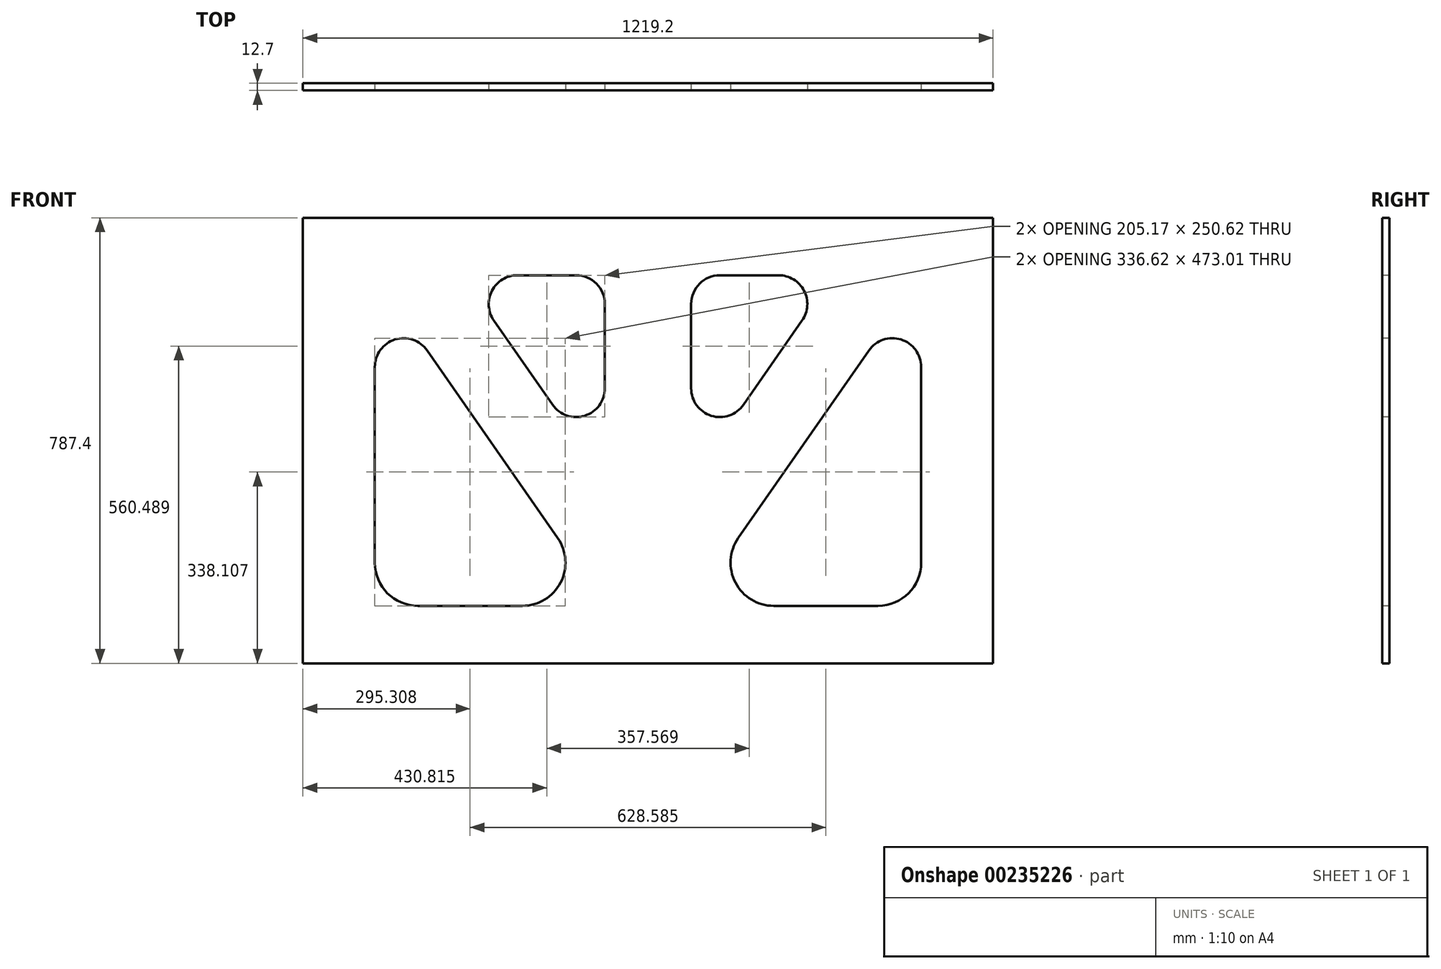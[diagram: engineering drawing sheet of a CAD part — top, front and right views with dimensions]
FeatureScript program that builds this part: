
annotation { "Feature Type Name" : "Feature", "Feature Type Description" : "" }
export const myFeature = defineFeature(function(context is Context, id is Id, definition is map)
    precondition{}
    {
        {
            var Q0;
            Q0=qCreatedBy(makeId("Front.planeOp"),FACE);
            var sketch = newSketch(context, id + "F0", { "sketchPlane" : qUnion([Q0])});
            skLineSegment(sketch, "E0.bottom", {"start": v(-609.6, 393.7) * mm, "end": v(609.6, 393.7) * mm});
            skLineSegment(sketch, "E0.top", {"start": v(-609.6, -393.7) * mm, "end": v(609.6, -393.7) * mm});
            skLineSegment(sketch, "E0.left", {"start": v(-609.6, 393.7) * mm, "end": v(-609.6, -393.7) * mm});
            skLineSegment(sketch, "E0.right", {"start": v(609.6, 393.7) * mm, "end": v(609.6, -393.7) * mm});
            skSolve(sketch);
        }
        {
            var Q0;
            Q0=makeQuery(id+"F0.imprint","IMPRINT",FACE,{"disambiguationData":[TD([[makeQuery(id+"F0.imprint","IMPRINT",EDGE,{"derivedFrom":sQuery(id+"F0.wireOp",EDGE,"E0.bottom")}),-1.0]])]});
            extrude(context, id + "F1", {"entities" : qUnion([Q0]), "depth" : 12.7 * mm});
        }
        {
            var Q0;
            Q0=makeQuery(id+"F1.opExtrude","CAP_FACE",FACE,{"disambiguationData":[OSD([sQuery(id+"F0.wireOp",EDGE,"E0.bottom"),sQuery(id+"F0.wireOp",EDGE,"E0.top"),sQuery(id+"F0.wireOp",EDGE,"E0.left"),sQuery(id+"F0.wireOp",EDGE,"E0.right")])],"isStart":false});
            var sketch = newSketch(context, id + "F2", { "sketchPlane" : qUnion([Q0])});
            skLineSegment(sketch, "E1", {"start": v(-482.6, 130.12) * mm, "end": v(-482.6, -215.9) * mm});
            skLineSegment(sketch, "E2", {"start": v(-406.4, -292.1) * mm, "end": v(-222.03, -292.1) * mm});
            skLineSegment(sketch, "E3", {"start": v(-159.48, -172.38) * mm, "end": v(-390.1, 159.13) * mm});
            skLineSegment(sketch, "E4", {"start": v(-272.37, 212.29) * mm, "end": v(-168.7, 63.26) * mm});
            skLineSegment(sketch, "E5", {"start": v(-76.2, 92.27) * mm, "end": v(-76.2, 241.3) * mm});
            skLineSegment(sketch, "E6", {"start": v(-127, 292.1) * mm, "end": v(-230.67, 292.1) * mm});
            skLineSegment(sketch, "E7", {"start": v(168.7, 63.26) * mm, "end": v(272.37, 212.29) * mm});
            skLineSegment(sketch, "E8", {"start": v(230.67, 292.1) * mm, "end": v(127, 292.1) * mm});
            skLineSegment(sketch, "E9", {"start": v(76.2, 241.3) * mm, "end": v(76.2, 92.27) * mm});
            skLineSegment(sketch, "E10", {"start": v(390.1, 159.13) * mm, "end": v(159.48, -172.38) * mm});
            skLineSegment(sketch, "E11", {"start": v(222.03, -292.1) * mm, "end": v(406.4, -292.1) * mm});
            skLineSegment(sketch, "E12", {"start": v(482.6, -215.9) * mm, "end": v(482.6, 130.12) * mm});
            skPoint(sketch, "E13.visualSharp", {"position": v(-482.6, 292.1) * mm});
            skArc(sketch, "E13.filletArc", {"start": v(-390.1, 159.13) * mm, "mid": v(-447, 178.6) * mm, "end": v(-482.6, 130.12) * mm});
            skPoint(sketch, "E14.visualSharp", {"position": v(-482.6, -292.1) * mm});
            skArc(sketch, "E14.filletArc", {"start": v(-482.6, -215.9) * mm, "mid": v(-460.28, -269.78) * mm, "end": v(-406.4, -292.1) * mm});
            skPoint(sketch, "E15.visualSharp", {"position": v(-76.2, -292.1) * mm});
            skArc(sketch, "E15.filletArc", {"start": v(-222.03, -292.1) * mm, "mid": v(-154.5, -251.19) * mm, "end": v(-159.48, -172.38) * mm});
            skPoint(sketch, "E16.visualSharp", {"position": v(-76.2, -69.7) * mm});
            skArc(sketch, "E16.filletArc", {"start": v(-168.7, 63.26) * mm, "mid": v(-111.8, 43.8) * mm, "end": v(-76.2, 92.27) * mm});
            skPoint(sketch, "E17.visualSharp", {"position": v(-327.9, 292.1) * mm});
            skArc(sketch, "E17.filletArc", {"start": v(-230.67, 292.1) * mm, "mid": v(-275.7, 264.83) * mm, "end": v(-272.37, 212.29) * mm});
            skPoint(sketch, "E18.visualSharp", {"position": v(-76.2, 292.1) * mm});
            skArc(sketch, "E18.filletArc", {"start": v(-76.2, 241.3) * mm, "mid": v(-91.08, 277.22) * mm, "end": v(-127, 292.1) * mm});
            skPoint(sketch, "E19.visualSharp", {"position": v(76.2, 292.1) * mm});
            skArc(sketch, "E19.filletArc", {"start": v(127, 292.1) * mm, "mid": v(91.08, 277.22) * mm, "end": v(76.2, 241.3) * mm});
            skPoint(sketch, "E20.visualSharp", {"position": v(327.9, 292.1) * mm});
            skArc(sketch, "E20.filletArc", {"start": v(272.37, 212.29) * mm, "mid": v(275.7, 264.83) * mm, "end": v(230.67, 292.1) * mm});
            skPoint(sketch, "E21.visualSharp", {"position": v(76.2, -69.7) * mm});
            skArc(sketch, "E21.filletArc", {"start": v(76.2, 92.27) * mm, "mid": v(111.8, 43.8) * mm, "end": v(168.7, 63.26) * mm});
            skPoint(sketch, "E22.visualSharp", {"position": v(76.2, -292.1) * mm});
            skArc(sketch, "E22.filletArc", {"start": v(159.48, -172.38) * mm, "mid": v(154.5, -251.19) * mm, "end": v(222.03, -292.1) * mm});
            skPoint(sketch, "E23.visualSharp", {"position": v(482.6, -292.1) * mm});
            skArc(sketch, "E23.filletArc", {"start": v(406.4, -292.1) * mm, "mid": v(460.28, -269.78) * mm, "end": v(482.6, -215.9) * mm});
            skPoint(sketch, "E24.visualSharp", {"position": v(482.6, 292.1) * mm});
            skArc(sketch, "E24.filletArc", {"start": v(482.6, 130.12) * mm, "mid": v(447, 178.6) * mm, "end": v(390.1, 159.13) * mm});
            skSolve(sketch);
        }
        {
            var Q0;
            Q0=makeQuery(id+"F2.imprint","IMPRINT",FACE,{"disambiguationData":[TD([[makeQuery(id+"F2.imprint","IMPRINT",EDGE,{"derivedFrom":sQuery(id+"F2.wireOp",EDGE,"E1")}),1.0]])]});
            var Q1;
            Q1=makeQuery(id+"F2.imprint","IMPRINT",FACE,{"disambiguationData":[TD([[makeQuery(id+"F2.imprint","IMPRINT",EDGE,{"derivedFrom":sQuery(id+"F2.wireOp",EDGE,"E4")}),1.0]])]});
            var Q2;
            Q2=makeQuery(id+"F2.imprint","IMPRINT",FACE,{"disambiguationData":[TD([[makeQuery(id+"F2.imprint","IMPRINT",EDGE,{"derivedFrom":sQuery(id+"F2.wireOp",EDGE,"E7")}),1.0]])]});
            var Q3;
            Q3=makeQuery(id+"F2.imprint","IMPRINT",FACE,{"disambiguationData":[TD([[makeQuery(id+"F2.imprint","IMPRINT",EDGE,{"derivedFrom":sQuery(id+"F2.wireOp",EDGE,"E10")}),1.0]])]});
            extrude(context, id + "F3", {"entities" : qUnion([Q0, Q1, Q2, Q3]), "operationType" : NewBodyOperationType.REMOVE, "endBound" : BoundingType.THROUGH_ALL, "oppositeDirection" : true, "depth" : 25.4 * mm});
        }
    });
